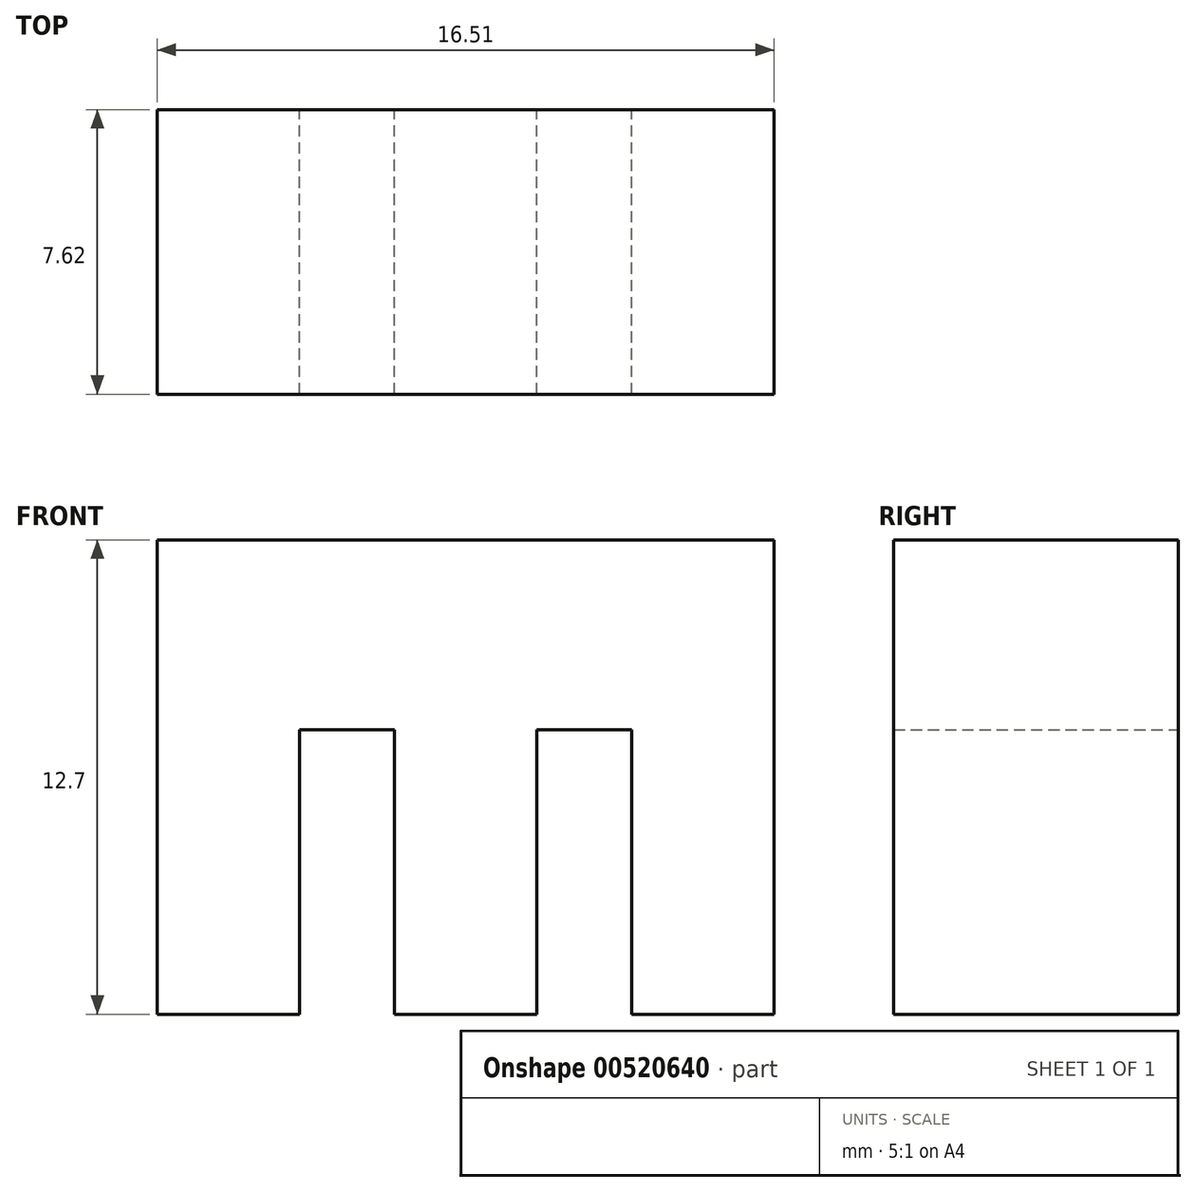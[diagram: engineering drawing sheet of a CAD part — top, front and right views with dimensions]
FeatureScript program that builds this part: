
annotation { "Feature Type Name" : "Feature", "Feature Type Description" : "" }
export const myFeature = defineFeature(function(context is Context, id is Id, definition is map)
    precondition{}
    {
        {
            var Q0;
            Q0=qCreatedBy(makeId("Front.planeOp"),FACE);
            var sketch = newSketch(context, id + "F0", { "sketchPlane" : qUnion([Q0])});
            skLineSegment(sketch, "E0", {"start": v(-12.7, 0) * mm, "end": v(-8.89, 0) * mm});
            skLineSegment(sketch, "E1", {"start": v(-8.89, 0) * mm, "end": v(-8.89, 7.62) * mm});
            skLineSegment(sketch, "E2", {"start": v(0, 7.62) * mm, "end": v(0, 0) * mm});
            skLineSegment(sketch, "E3", {"start": v(0, 0) * mm, "end": v(3.8, 0) * mm});
            skLineSegment(sketch, "E4", {"start": v(3.8, 0) * mm, "end": v(3.8, 12.7) * mm});
            skLineSegment(sketch, "E5", {"start": v(-12.7, 12.7) * mm, "end": v(-12.7, 0) * mm});
            skPoint(sketch, "E6.endSnap0", {"position": v(3.8, 6.35) * mm});
            skLineSegment(sketch, "E7", {"start": v(-8.9, 7.62) * mm, "end": v(-6.35, 7.62) * mm});
            skLineSegment(sketch, "E8", {"start": v(-6.35, 7.62) * mm, "end": v(-6.35, 0) * mm});
            skLineSegment(sketch, "E9", {"start": v(-6.35, 0) * mm, "end": v(-2.54, 0) * mm});
            skLineSegment(sketch, "E10", {"start": v(-2.54, 0) * mm, "end": v(-2.54, 7.62) * mm});
            skLineSegment(sketch, "E11", {"start": v(-2.54, 7.62) * mm, "end": v(0, 7.62) * mm});
            skLineSegment(sketch, "E12", {"start": v(-12.7, 12.7) * mm, "end": v(3.8, 12.7) * mm});
            skSolve(sketch);
        }
        {
            var Q0;
            Q0=qSketchRegion(id+"F0",true);
            extrude(context, id + "F1", {"entities" : qUnion([Q0]), "depth" : 7.62 * mm, "offsetDistance" : 25.4 * mm});
        }
    });
